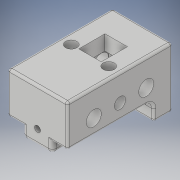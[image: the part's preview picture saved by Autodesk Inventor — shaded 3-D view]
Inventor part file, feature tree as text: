
AUTODESK INVENTOR PART (.ipt)
format: ipt  version: 2019 (Build 230136000, 136)  size: 316,416 bytes
history: native  units: mm
features: sketch x10, fillet x7, extrude x6, hole x5
ambient origin geometry x8: Origin, YZ Plane, XZ Plane, XY Plane, X Axis, Y Axis, Z Axis, Center Point
bodies: Solid1 (feature_tree)
feature tree (28):
  extrude  "Extrusion1"  Depth=80.0mm
  extrude  "Extrusion4"  Depth=20.0mm
  extrude  "Extrusion11"  Depth=20.0mm TaperAngle=0.0deg
  sketch  "Sketch13"  dims[d56=20.0mm d57=110.0mm]
  hole  "Hole2"  [1 undecoded]
  hole  "Hole3"  [1 undecoded]
  extrude  "Extrusion12"  Depth=35.0mm
  fillet  "Fillet10"  Radius=45.0mm
  hole  "Hole4"  [1 undecoded]
  extrude  "Extrusion13"  Depth=15.0mm
  hole  "Hole5"  [1 undecoded]
  fillet  "Fillet12"  Radius=30.0mm
  fillet  "Fillet13"  Radius=5.0mm
  fillet  "Fillet14"  Radius=5.0mm
  extrude  "Extrusion14"  Depth=15.0mm
  fillet  "Fillet15"  Radius=35.0mm
  fillet  "Fillet16"  Radius=3.0mm
  fillet  "Fillet18"  Radius=3.0mm
  hole  "Hole6"  [1 undecoded]
  sketch  "Sketch1"  dims[d0=140.0mm d1=80.0mm]
  sketch  "Sketch5"  dims[d2=20.0mm d3=0.0mm d30=35.0mm]
  sketch  "Sketch12"  dims[d31=30.0mm d32=20.0mm d33=0.0mm]
  sketch  "Sketch14"  dims[d58=35.0mm d59=0.0mm d60=15.0mm]
  sketch  "Sketch15"  dims[d61=35.0mm d62=35.0mm]
  sketch  "Sketch16"  dims[d63=20.0mm d64=6.0mm d65=4.0mm d66=2.0mm d67=90.0deg d68=8.0mm d69=20.594885mm]
  sketch  "Sketch17"  dims[d70=15.0mm d71=6.0mm d72=4.0mm d73=2.0mm d74=90.0deg d75=8.0mm d76=20.594885mm d77=45.0mm]
  sketch  "Sketch18"  dims[d78=60.0mm d79=0.0mm d81=10.0mm]
  sketch  "Sketch19"  dims[d82=30.0mm d83=8.0mm d84=6.0mm d85=4.0mm d86=2.0mm d87=90.0deg d88=8.0mm d89=20.594885mm d91=45.0mm d92=50.0mm d93=0.0mm d94=30.0mm d95=8.0mm d96=6.0mm d97=4.0mm d98=2.0mm d99=90.0deg d100=8.0mm d101=20.594885mm d102=5.0mm d103=5.0mm d104=5.0mm d105=35.0mm d106=0.0mm d107=3.0mm d108=3.0mm d110=3.0mm d111=25.0mm d112=25.0mm d113=15.0mm d114=6.0mm d115=4.0mm d116=2.0mm d117=90.0deg d118=15.0mm d119=0.0mm d12=1.0mm d13=1.0mm d14=1.0mm d15=0.15mm d16=0.25mm d17=0.375mm d18=14.3117mm d19=0.75mm d20=20.594885mm d21=0.0625mm d22=0.75mm d23=0.375mm]
note: 5 required parameter values undecoded (feature->parameter linkage not recoverable at this tier; creation-order binding heuristic only, values carry confidence <= 0.55)
